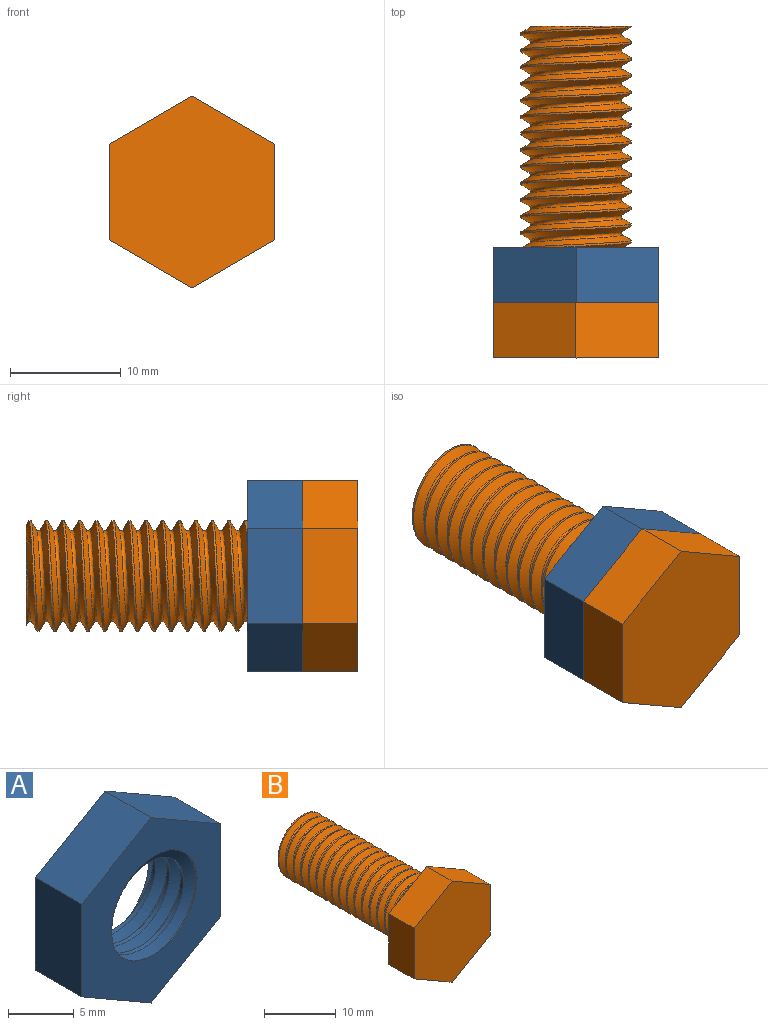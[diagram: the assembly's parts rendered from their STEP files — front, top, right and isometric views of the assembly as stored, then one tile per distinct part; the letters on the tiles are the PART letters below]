
ASSEMBLY  parts=2 mates=1
PART A: 12 faces, bbox 15.4x6.8x17.8 mm
  f0: plane 17.76x15.44mm, normal (0,1,0), area 127.8mm2, adj f2,f3,f4,f5,f6,f7,f8,f9
  f1: plane 17.76x15.44mm, normal (0,-1,0), area 127.8mm2, adj f2,f3,f4,f5,f6,f7,f8,f9
  f2: plane 7.5x5mm, normal (-0.5,0,0.87), area 43.3mm2, adj f0,f1,f3,f7
  f3: plane 7.5x5mm, normal (0.5,0,0.87), area 43.3mm2, adj f0,f1,f2,f4
  f4: plane 8.66x5mm, normal (1,0,0), area 43.3mm2, adj f0,f1,f3,f5
  f5: plane 7.5x5mm, normal (0.5,0,-0.87), area 43.3mm2, adj f0,f1,f4,f6
  f6: plane 7.5x5mm, normal (-0.5,0,-0.87), area 43.3mm2, adj f0,f1,f5,f7
  f7: plane 8.66x5mm, normal (-1,0,0), area 43.3mm2, adj f0,f1,f2,f6
  f8: bspline ~11.69x10.12mm, area 91.2mm2, adj f0,f1,f10,f11
  f9: bspline ~11.69x10.12mm, area 91.5mm2, adj f0,f1,f10,f11
  f10: bspline ~11.85x10.26mm, area 23.2mm2, adj f0,f1,f8,f9
  f11: cylinder r=4.25mm len=8.5mm, axis (0,1,0), area 32.9mm2, adj f0,f1,f8,f9
PART B: 13 faces, bbox 15.4x31.1x17.7 mm
  f0: cylinder r=5mm len=25mm, axis (0,-1,0), area 134.5mm2, adj f1,f9,f11,f12
  f1: plane 9.53x9.48mm, normal (0,1,0), area 64.8mm2, adj f0,f10,f11,f12
  f2: plane 7.5x5mm, normal (-0.5,0,0.87), area 43.3mm2, adj f3,f7,f8,f9
  f3: plane 8.66x5mm, normal (-1,0,0), area 43.3mm2, adj f2,f4,f8,f9
  f4: plane 7.5x5mm, normal (-0.5,0,-0.87), area 43.3mm2, adj f3,f5,f8,f9
  f5: plane 7.5x5mm, normal (0.5,0,-0.87), area 43.3mm2, adj f4,f6,f8,f9
  f6: plane 8.66x5mm, normal (1,0,0), area 43.3mm2, adj f5,f7,f8,f9
  f7: plane 7.5x5mm, normal (0.5,0,0.87), area 43.3mm2, adj f2,f6,f8,f9
  f8: plane 17.32x15mm, normal (0,-1,0), area 194.9mm2, adj f2,f3,f4,f5,f6,f7
  f9: plane 17.74x15.42mm, normal (0,1,0), area 130.1mm2, adj f0,f2,f3,f4,f5,f6,f7,f10
  f10: bspline ~26.13x9.67mm, area 182.1mm2, adj f1,f9,f11,f12
  f11: bspline ~26.22x11.55mm, area 451.7mm2, adj f0,f1,f9,f10
  f12: bspline ~26.22x11.55mm, area 451.1mm2, adj f0,f1,f9,f10
PLACE A rot(axis=(0,1,0),120deg) t=(6.18,8.31,-10.02)mm
PLACE B t=(6.18,8.31,-10.02)mm fixed
MATE cylindrical B.f0 <-> A.f11  axis (0,-1,0) through (6.18,3.31,-10.02)mm
